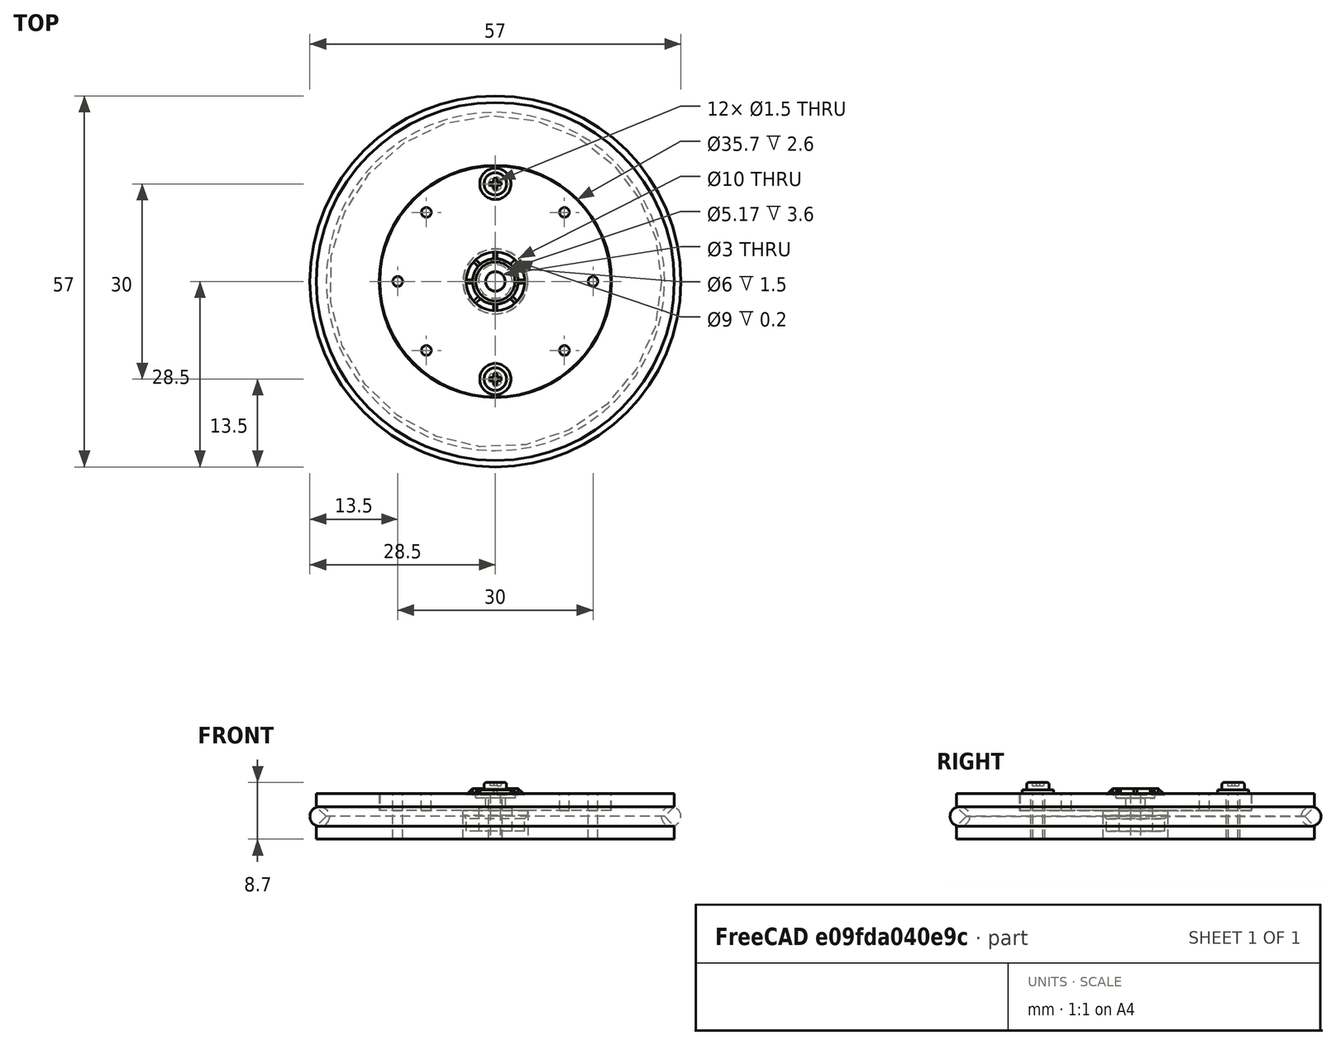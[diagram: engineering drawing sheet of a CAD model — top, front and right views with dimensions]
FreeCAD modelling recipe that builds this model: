
FCSTD DOCUMENT  (FreeCAD 0.14R3702 (Git))
Label: Miniskybot-wheel-futaba3003-rounded-big-horn-assembly
License: CC-BY 3.0
LicenseURL: http://creativecommons.org/licenses/by/3.0/
objects: Part::Feature×4, Part::Torus×1, Part::Compound×1
note: 6 computed .brp shape members not serialized (recipe doc carries the construction recipe); baked Part::Feature solids carry a one-line shape summary decoded from their .brp

FEATURE [Part::Feature] Pocket  label="Wheel-futaba3003-rounded-big-horn"
  shape: bbox 55 x 55 x 7.002 mm, 13 faces (baked)
FEATURE [Part::Feature] PolarPattern001  label="big-rounded-horn-final001"
  Placement = pos=(0,0,0.9) rot=(0,0,1;0rad)
  shape: bbox 35.5 x 35.5 x 6.6 mm, 65 faces (baked)
FEATURE [Part::Torus] Torus  label="o-ring"
  Angle1 = -180
  Angle2 = 180
  Angle3 = 360
  Radius1 = 27
  Radius2 = 1.5
FEATURE [Part::Feature] Fillet  label="bolt-1"
  Placement = pos=(0,15,3.5) rot=(0,0,1;0rad)
  shape: bbox 4.8 x 4.8 x 8.7 mm, 21 faces (baked)
FEATURE [Part::Feature] Fillet001  label="bolt-002"
  Placement = pos=(0,-15,3.5) rot=(0,0,1;0rad)
  shape: bbox 4.8 x 4.8 x 8.7 mm, 21 faces (baked)
FEATURE [Part::Compound] Compound  label="Miniskybot-wheel-futaba3003-rounded-big-horn-assembly"
  Links = -> [Pocket,PolarPattern001,Torus,Fillet,Fillet001]
